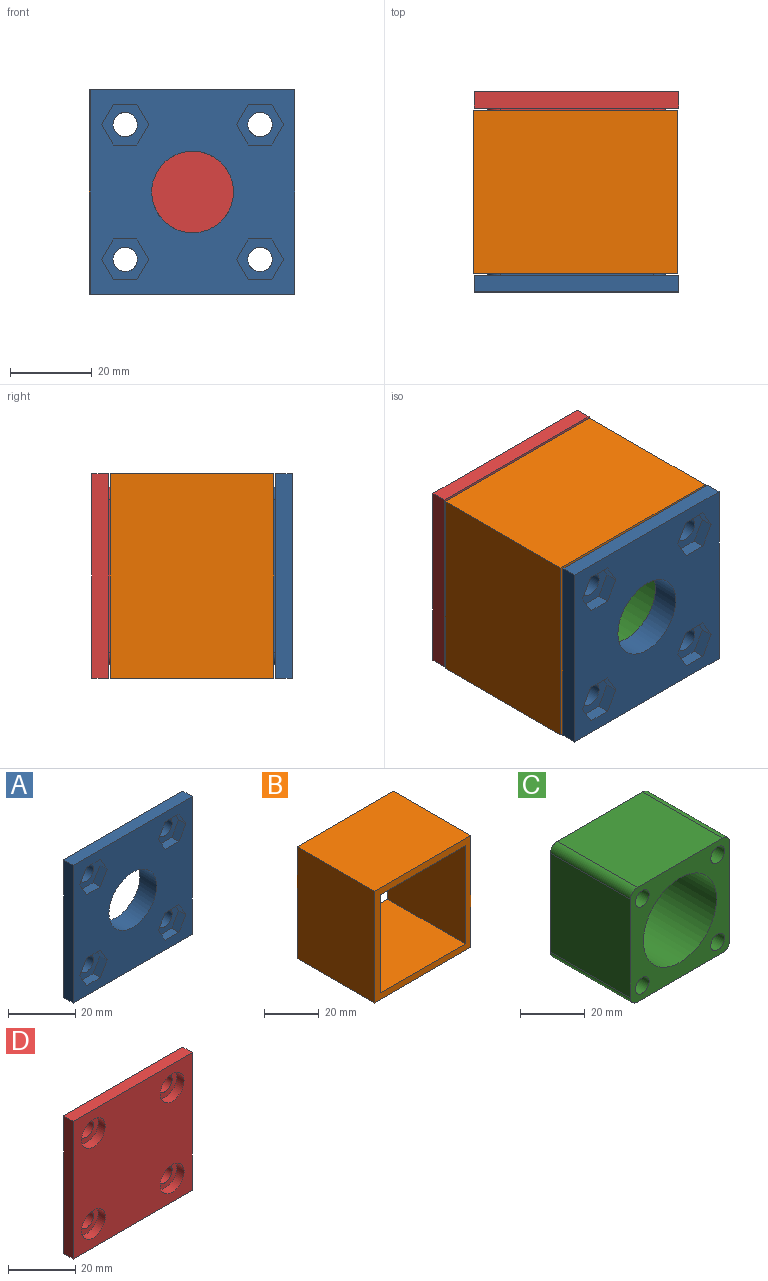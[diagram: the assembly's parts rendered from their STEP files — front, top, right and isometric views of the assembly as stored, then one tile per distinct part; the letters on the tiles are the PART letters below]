
ASSEMBLY  parts=4 mates=3
PART A: 48 faces, bbox 50x7x50 mm
  f0: plane 50x50mm, normal (0,-1,0), area 1839.4mm2, adj f2,f3,f4,f5,f15,f16,f17,f18
  f1: plane 50x50mm, normal (0,1,0), area 624.2mm2, adj f2,f3,f4,f5,f6,f7,f8,f9
  f2: plane 50x4mm, normal (-1,0,0), area 200mm2, adj f0,f1,f3,f5
  f3: plane 50x4mm, normal (0,0,-1), area 200mm2, adj f0,f1,f2,f4
  f4: plane 50x4mm, normal (1,0,0), area 200mm2, adj f0,f1,f3,f5
  f5: plane 50x4mm, normal (0,0,1), area 200mm2, adj f0,f1,f2,f4
  f6: plane 37.4x3mm, normal (1,0,0), area 112.2mm2, adj f1,f10,f44,f47
  f7: plane 37.4x3mm, normal (0,0,-1), area 112.2mm2, adj f1,f10,f44,f45
  f8: plane 37.4x3mm, normal (-1,0,0), area 112.2mm2, adj f1,f10,f45,f46
  f9: plane 37.4x3mm, normal (0,0,1), area 112.2mm2, adj f1,f10,f46,f47
  f10: plane 43.4x43.4mm, normal (0,1,0), area 1448.6mm2, adj f6,f7,f8,f9,f11,f12,f13,f14
  f11: cylinder r=3mm len=6mm, axis (0,1,0), area 75.4mm2, adj f10,f29
  f12: cylinder r=3mm len=6mm, axis (0,1,0), area 75.4mm2, adj f10,f22
  f13: cylinder r=3mm len=6mm, axis (0,1,0), area 75.4mm2, adj f10,f43
  f14: cylinder r=3mm len=6mm, axis (0,1,0), area 75.4mm2, adj f10,f36
  f15: cylinder r=10mm len=20mm, axis (0,1,0), area 439.8mm2, adj f0,f10
  f16: plane 5x3mm, normal (-0.87,0,0.5), area 17.3mm2, adj f0,f17,f21,f22
  f17: plane 5x3mm, normal (-0.87,0,-0.5), area 17.3mm2, adj f0,f16,f18,f22
  f18: plane 5.77x3mm, normal (0,0,-1), area 17.3mm2, adj f0,f17,f19,f22
  f19: plane 5x3mm, normal (0.87,0,-0.5), area 17.3mm2, adj f0,f18,f20,f22
  f20: plane 5x3mm, normal (0.87,0,0.5), area 17.3mm2, adj f0,f19,f21,f22
  f21: plane 5.77x3mm, normal (0,0,1), area 17.3mm2, adj f0,f16,f20,f22
  f22: plane 11.55x10mm, normal (0,-1,0), area 58.3mm2, adj f12,f16,f17,f18,f19,f20,f21
  f23: plane 5x3mm, normal (0.87,0,-0.5), area 17.3mm2, adj f0,f24,f28,f29
  f24: plane 5x3mm, normal (0.87,0,0.5), area 17.3mm2, adj f0,f23,f25,f29
  f25: plane 5.77x3mm, normal (0,0,1), area 17.3mm2, adj f0,f24,f26,f29
  f26: plane 5x3mm, normal (-0.87,0,0.5), area 17.3mm2, adj f0,f25,f27,f29
  f27: plane 5x3mm, normal (-0.87,0,-0.5), area 17.3mm2, adj f0,f26,f28,f29
  f28: plane 5.77x3mm, normal (0,0,-1), area 17.3mm2, adj f0,f23,f27,f29
  f29: plane 11.55x10mm, normal (0,-1,0), area 58.3mm2, adj f11,f23,f24,f25,f26,f27,f28
  f30: plane 5x3mm, normal (-0.87,0,0.5), area 17.3mm2, adj f0,f31,f35,f36
  f31: plane 5x3mm, normal (-0.87,0,-0.5), area 17.3mm2, adj f0,f30,f32,f36
  f32: plane 5.77x3mm, normal (0,0,-1), area 17.3mm2, adj f0,f31,f33,f36
  f33: plane 5x3mm, normal (0.87,0,-0.5), area 17.3mm2, adj f0,f32,f34,f36
  f34: plane 5x3mm, normal (0.87,0,0.5), area 17.3mm2, adj f0,f33,f35,f36
  f35: plane 5.77x3mm, normal (0,0,1), area 17.3mm2, adj f0,f30,f34,f36
  f36: plane 11.55x10mm, normal (0,-1,0), area 58.3mm2, adj f14,f30,f31,f32,f33,f34,f35
  f37: plane 5x3mm, normal (-0.87,0,0.5), area 17.3mm2, adj f0,f38,f42,f43
  f38: plane 5x3mm, normal (-0.87,0,-0.5), area 17.3mm2, adj f0,f37,f39,f43
  f39: plane 5.77x3mm, normal (0,0,-1), area 17.3mm2, adj f0,f38,f40,f43
  f40: plane 5x3mm, normal (0.87,0,-0.5), area 17.3mm2, adj f0,f39,f41,f43
  f41: plane 5x3mm, normal (0.87,0,0.5), area 17.3mm2, adj f0,f40,f42,f43
  f42: plane 5.77x3mm, normal (0,0,1), area 17.3mm2, adj f0,f37,f41,f43
  f43: plane 11.55x10mm, normal (0,-1,0), area 58.3mm2, adj f13,f37,f38,f39,f40,f41,f42
  f44: cylinder r=3mm len=3mm, axis (0,-1,0), area 14.1mm2, adj f1,f6,f7,f10
  f45: cylinder r=3mm len=3mm, axis (0,1,0), area 14.1mm2, adj f1,f7,f8,f10
  f46: cylinder r=3mm len=3mm, axis (0,-1,0), area 14.1mm2, adj f1,f8,f9,f10
  f47: cylinder r=3mm len=3mm, axis (0,1,0), area 14.1mm2, adj f1,f6,f9,f10
PART B: 10 faces, bbox 50x40x50 mm
  f0: plane 50x40mm, normal (-1,0,0), area 2000mm2, adj f1,f7,f8,f9
  f1: plane 50x40mm, normal (0,0,-1), area 2000mm2, adj f0,f2,f8,f9
  f2: plane 50x40mm, normal (1,0,0), area 2000mm2, adj f1,f7,f8,f9
  f3: plane 44x40mm, normal (0,0,1), area 1760mm2, adj f4,f6,f8,f9
  f4: plane 44x40mm, normal (1,0,0), area 1760mm2, adj f3,f5,f8,f9
  f5: plane 44x40mm, normal (0,0,-1), area 1760mm2, adj f4,f6,f8,f9
  f6: plane 44x40mm, normal (-1,0,0), area 1760mm2, adj f3,f5,f8,f9
  f7: plane 50x40mm, normal (0,0,1), area 2000mm2, adj f0,f2,f8,f9
  f8: plane 50x50mm, normal (0,-1,0), area 564mm2, adj f0,f1,f2,f3,f4,f5,f6,f7
  f9: plane 50x50mm, normal (0,1,0), area 564mm2, adj f0,f1,f2,f3,f4,f5,f6,f7
PART C: 19 faces, bbox 43.4x35x43.4 mm
  f0: cylinder r=16mm len=32mm, axis (0,1,0), area 3041.1mm2, adj f10,f13
  f1: plane 37.4x35mm, normal (-1,0,0), area 1309mm2, adj f10,f11,f15,f18
  f2: plane 37.4x35mm, normal (0,0,-1), area 1309mm2, adj f10,f11,f15,f16
  f3: plane 37.4x35mm, normal (1,0,0), area 1309mm2, adj f10,f11,f16,f17
  f4: cylinder r=16mm len=32mm, axis (0,1,0), area 276.5mm2, adj f11,f14
  f5: cylinder r=3mm len=35mm, axis (0,1,0), area 659.7mm2, adj f10,f11
  f6: cylinder r=3mm len=35mm, axis (0,1,0), area 659.7mm2, adj f10,f11
  f7: cylinder r=3mm len=35mm, axis (0,1,0), area 659.7mm2, adj f10,f11
  f8: cylinder r=3mm len=35mm, axis (0,1,0), area 659.7mm2, adj f10,f11
  f9: plane 37.4x35mm, normal (0,0,1), area 1309mm2, adj f10,f11,f17,f18
  f10: plane 43.4x43.4mm, normal (0,-1,0), area 958.5mm2, adj f0,f1,f2,f3,f5,f6,f7,f8
  f11: plane 43.4x43.4mm, normal (0,1,0), area 958.5mm2, adj f1,f2,f3,f4,f5,f6,f7,f8
  f12: cylinder r=14mm len=28mm, axis (0,1,0), area 175.9mm2, adj f13,f14
  f13: plane 32x32mm, normal (0,-1,0), area 188.5mm2, adj f0,f12
  f14: plane 32x32mm, normal (0,1,0), area 188.5mm2, adj f4,f12
  f15: cylinder r=3mm len=35mm, axis (0,1,0), area 164.9mm2, adj f1,f2,f10,f11
  f16: cylinder r=3mm len=35mm, axis (0,-1,0), area 164.9mm2, adj f2,f3,f10,f11
  f17: cylinder r=3mm len=35mm, axis (0,1,0), area 164.9mm2, adj f3,f9,f10,f11
  f18: cylinder r=3mm len=35mm, axis (0,-1,0), area 164.9mm2, adj f1,f9,f10,f11
PART D: 27 faces, bbox 50x7x50 mm
  f0: plane 50x50mm, normal (0,1,0), area 624.2mm2, adj f1,f2,f3,f4,f6,f7,f8,f9
  f1: plane 50x4mm, normal (-1,0,0), area 200mm2, adj f0,f2,f4,f5
  f2: plane 50x4mm, normal (0,0,-1), area 200mm2, adj f0,f1,f3,f5
  f3: plane 50x4mm, normal (1,0,0), area 200mm2, adj f0,f2,f4,f5
  f4: plane 50x4mm, normal (0,0,1), area 200mm2, adj f0,f1,f3,f5
  f5: plane 50x50mm, normal (0,-1,0), area 2185.8mm2, adj f1,f2,f3,f4,f15,f17,f19,f21
  f6: plane 37.4x3mm, normal (1,0,0), area 112.2mm2, adj f0,f10,f23,f26
  f7: plane 37.4x3mm, normal (0,0,-1), area 112.2mm2, adj f0,f10,f23,f24
  f8: plane 37.4x3mm, normal (-1,0,0), area 112.2mm2, adj f0,f10,f24,f25
  f9: plane 37.4x3mm, normal (0,0,1), area 112.2mm2, adj f0,f10,f25,f26
  f10: plane 43.4x43.4mm, normal (0,1,0), area 1762.7mm2, adj f6,f7,f8,f9,f11,f12,f13,f14
  f11: cylinder r=3mm len=6mm, axis (0,1,0), area 75.4mm2, adj f10,f22
  f12: cylinder r=3mm len=6mm, axis (0,1,0), area 75.4mm2, adj f10,f20
  f13: cylinder r=3mm len=6mm, axis (0,1,0), area 75.4mm2, adj f10,f18
  f14: cylinder r=3mm len=6mm, axis (0,1,0), area 75.4mm2, adj f10,f16
  f15: cylinder r=5mm len=10mm, axis (0,-1,0), area 94.2mm2, adj f5,f16
  f16: plane 10x10mm, normal (0,-1,0), area 50.3mm2, adj f14,f15
  f17: cylinder r=5mm len=10mm, axis (0,-1,0), area 94.2mm2, adj f5,f18
  f18: plane 10x10mm, normal (0,-1,0), area 50.3mm2, adj f13,f17
  f19: cylinder r=5mm len=10mm, axis (0,-1,0), area 94.2mm2, adj f5,f20
  f20: plane 10x10mm, normal (0,-1,0), area 50.3mm2, adj f12,f19
  f21: cylinder r=5mm len=10mm, axis (0,-1,0), area 94.2mm2, adj f5,f22
  f22: plane 10x10mm, normal (0,-1,0), area 50.3mm2, adj f11,f21
  f23: cylinder r=3mm len=3mm, axis (0,-1,0), area 14.1mm2, adj f0,f6,f7,f10
  f24: cylinder r=3mm len=3mm, axis (0,1,0), area 14.1mm2, adj f0,f7,f8,f10
  f25: cylinder r=3mm len=3mm, axis (0,-1,0), area 14.1mm2, adj f0,f8,f9,f10
  f26: cylinder r=3mm len=3mm, axis (0,1,0), area 14.1mm2, adj f0,f6,f9,f10
PLACE A t=(-6.9,-7.15,22.46)mm
PLACE B t=(-7.2,17.35,22.46)mm
PLACE C t=(-6.9,17.35,22.46)mm
PLACE D rot(axis=(1,0,0),180deg) t=(-6.9,41.85,22.46)mm
MATE fastened D.f10 <-> C.f0  axis (0,-1,0) through (-6.9,34.85,22.46)mm
MATE fastened C.f3 <-> B.f6  axis (1,0,0) through (14.8,17.35,22.46)mm
MATE fastened A.f11 <-> C.f6  axis (0,1,0) through (9.6,-0.15,38.96)mm
